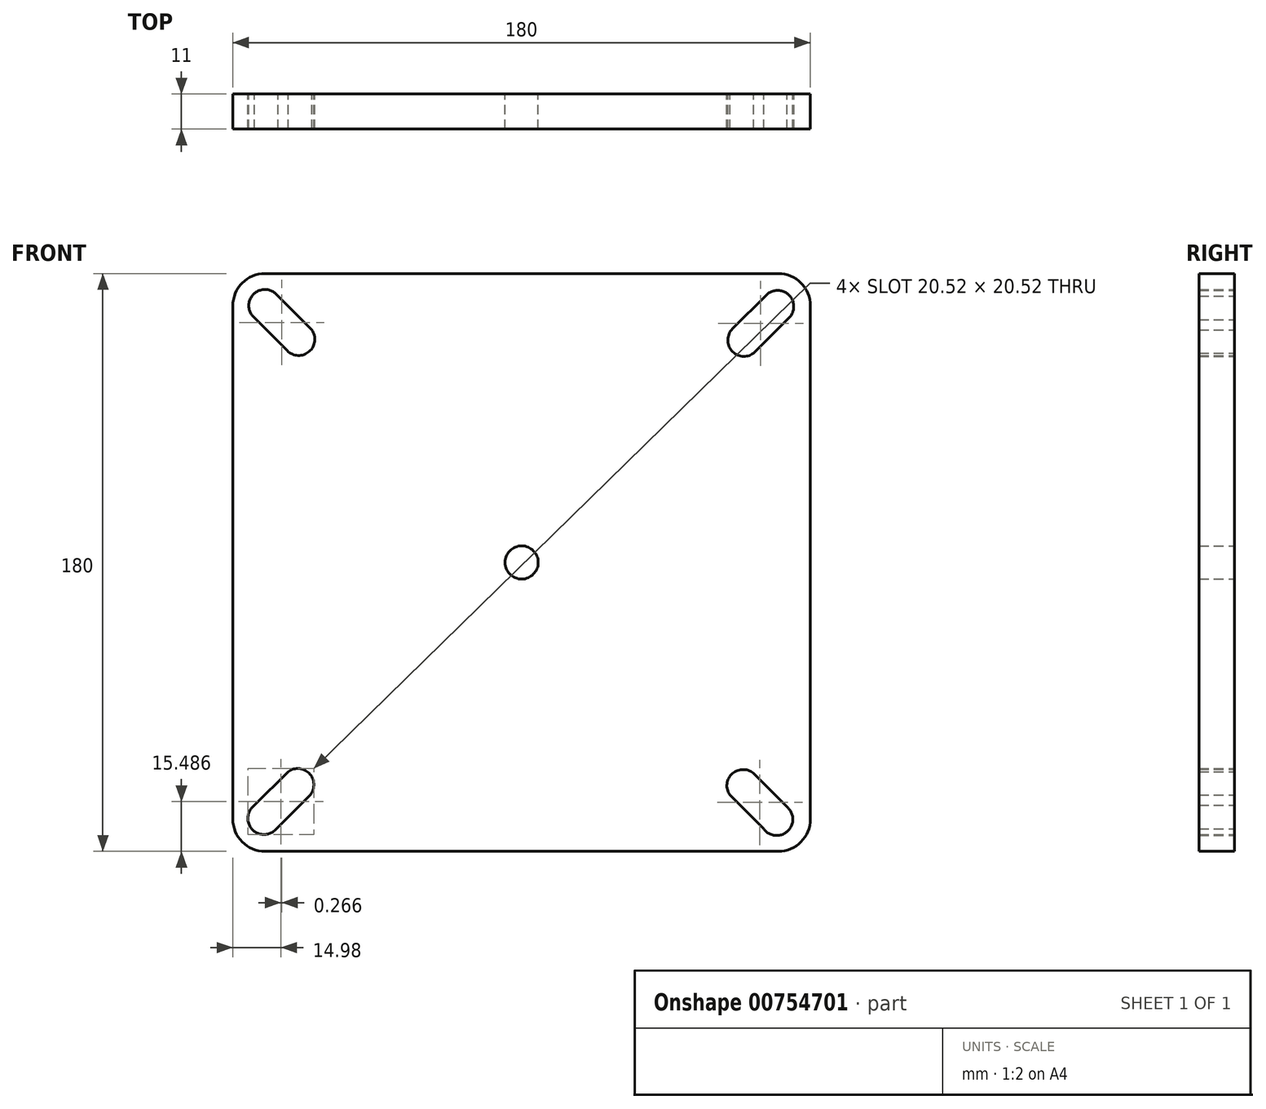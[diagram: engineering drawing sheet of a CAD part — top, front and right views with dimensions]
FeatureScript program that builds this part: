
annotation { "Feature Type Name" : "Feature", "Feature Type Description" : "" }
export const myFeature = defineFeature(function(context is Context, id is Id, definition is map)
    precondition{}
    {
        {
            var Q0;
            Q0=qCreatedBy(makeId("Front.planeOp"),FACE);
            var sketch = newSketch(context, id + "F0", { "sketchPlane" : qUnion([Q0])});
            skLineSegment(sketch, "E0.bottom", {"start": v(-79.75, 90) * mm, "end": v(80.25, 90) * mm});
            skLineSegment(sketch, "E0.top", {"start": v(-79.75, -90) * mm, "end": v(80.25, -90) * mm});
            skLineSegment(sketch, "E0.left", {"start": v(-89.75, 80) * mm, "end": v(-89.75, -80) * mm});
            skLineSegment(sketch, "E0.right", {"start": v(90.25, 80) * mm, "end": v(90.25, -80) * mm});
            skPoint(sketch, "E1.visualSharp", {"position": v(-89.75, 90) * mm});
            skArc(sketch, "E1.filletArc", {"start": v(-79.75, 90) * mm, "mid": v(-86.82, 87.08) * mm, "end": v(-89.75, 80) * mm});
            skPoint(sketch, "E2.visualSharp", {"position": v(90.25, 90) * mm});
            skArc(sketch, "E2.filletArc", {"start": v(90.25, 80) * mm, "mid": v(87.32, 87.08) * mm, "end": v(80.25, 90) * mm});
            skPoint(sketch, "E3.visualSharp", {"position": v(-89.75, -90) * mm});
            skArc(sketch, "E3.filletArc", {"start": v(-89.75, -80) * mm, "mid": v(-86.82, -87.06) * mm, "end": v(-79.75, -90) * mm});
            skPoint(sketch, "E4.visualSharp", {"position": v(90.25, -90) * mm});
            skArc(sketch, "E4.filletArc", {"start": v(80.25, -90) * mm, "mid": v(87.32, -87.06) * mm, "end": v(90.25, -80) * mm});
            skCircle(sketch, "E5", {"center": v(0.25, 0) * mm, "radius": 5.18 * mm});
            skPoint(sketch, "E5.centerSnap0", {"position": v(0.25, -90) * mm});
            skPoint(sketch, "E5.centerSnap1", {"position": v(-89.75, 0) * mm});
            skLineSegment(sketch, "E6", {"start": v(-79.75, 80) * mm, "end": v(0.25, 0) * mm, "construction": true});
            skLineSegment(sketch, "E7", {"start": v(0.25, 0) * mm, "end": v(80.25, 80) * mm, "construction": true});
            skLineSegment(sketch, "E8", {"start": v(0, 0) * mm, "end": v(80.25, -80) * mm, "construction": true});
            skLineSegment(sketch, "E9", {"start": v(0.25, 0) * mm, "end": v(-79.75, -80) * mm, "construction": true});
            skLineSegment(sketch, "E10", {"start": v(-83.3, 76.48) * mm, "end": v(-72.8, 65.98) * mm});
            skLineSegment(sketch, "E11", {"start": v(-75.67, 83) * mm, "end": v(-65.18, 72.5) * mm});
            skArc(sketch, "E12", {"start": v(-83.3, 76.48) * mm, "mid": v(-83, 83.85) * mm, "end": v(-75.67, 83) * mm});
            skArc(sketch, "E13", {"start": v(-72.8, 65.98) * mm, "mid": v(-65.97, 65.72) * mm, "end": v(-65.18, 72.5) * mm});
            skArc(sketch, "E14.1.0", {"start": v(76.48, 83.3) * mm, "mid": v(83.85, 83) * mm, "end": v(83, 75.67) * mm});
            skLineSegment(sketch, "E14.1.1", {"start": v(83, 75.67) * mm, "end": v(72.5, 65.18) * mm});
            skArc(sketch, "E14.1.2", {"start": v(65.98, 72.8) * mm, "mid": v(65.72, 65.97) * mm, "end": v(72.5, 65.18) * mm});
            skLineSegment(sketch, "E14.1.3", {"start": v(76.48, 83.3) * mm, "end": v(65.98, 72.8) * mm});
            skArc(sketch, "E14.2.0", {"start": v(83.3, -76.48) * mm, "mid": v(83, -83.85) * mm, "end": v(75.67, -83) * mm});
            skLineSegment(sketch, "E14.2.1", {"start": v(75.67, -83) * mm, "end": v(65.18, -72.5) * mm});
            skArc(sketch, "E14.2.2", {"start": v(72.8, -65.98) * mm, "mid": v(65.97, -65.72) * mm, "end": v(65.18, -72.5) * mm});
            skLineSegment(sketch, "E14.2.3", {"start": v(83.3, -76.48) * mm, "end": v(72.8, -65.98) * mm});
            skArc(sketch, "E14.3.0", {"start": v(-76.48, -83.3) * mm, "mid": v(-83.85, -83) * mm, "end": v(-83, -75.67) * mm});
            skLineSegment(sketch, "E14.3.1", {"start": v(-83, -75.67) * mm, "end": v(-72.5, -65.18) * mm});
            skArc(sketch, "E14.3.2", {"start": v(-65.98, -72.8) * mm, "mid": v(-65.72, -65.97) * mm, "end": v(-72.5, -65.18) * mm});
            skLineSegment(sketch, "E14.3.3", {"start": v(-76.48, -83.3) * mm, "end": v(-65.98, -72.8) * mm});
            skPoint(sketch, "E14.center", {"position": v(0, 0) * mm});
            skLineSegment(sketch, "E14.anchor1", {"start": v(0, 0) * mm, "end": v(-83.3, 76.48) * mm, "construction": true});
            skLineSegment(sketch, "E14.anchor2", {"start": v(0, 0) * mm, "end": v(-76.48, -83.3) * mm, "construction": true});
            skSolve(sketch);
        }
        {
            var Q0;
            Q0=makeQuery(id+"F0.imprint","IMPRINT",FACE,{"disambiguationData":[TD([[makeQuery(id+"F0.imprint","IMPRINT",EDGE,{"derivedFrom":sQuery(id+"F0.wireOp",EDGE,"E0.bottom")}),-1.0]])]});
            extrude(context, id + "F1", {"entities" : qUnion([Q0]), "depth" : 11 * mm, "offsetDistance" : 25 * mm});
        }
    });
